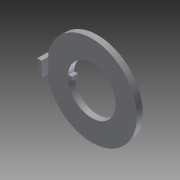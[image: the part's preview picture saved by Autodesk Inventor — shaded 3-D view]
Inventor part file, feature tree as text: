
AUTODESK INVENTOR PART (.ipt)
format: ipt  version: 2014 (Build 180170000, 170)  size: 108,032 bytes
history: native  units: in
note: dims shown in document units (in); Inventor stores cm internally (conversion verified against a paired STEP export)
features: other x7, extrude x2, sketch x2
ambient origin geometry x8: Origin, YZ Plane, XZ Plane, XY Plane, X Axis, Y Axis, Z Axis, Center Point
bodies: Solid1 (feature_tree)
feature tree (11):
  extrude  "Extrusion1"  Depth=0.079in TaperAngle=0.0deg
  extrude  "Extrusion2"  [1 undecoded]
  other  "ring_XY"
  other  "ring_YZ"
  other  "ring_ZX"
  other  "ring_X"
  other  "ring_Y"
  other  "ring_Z"
  other  "ring_Center"
  sketch  "Sketch_4"
  sketch  "Sketch_2"  dims[d0=0.031in d1=0.0in d2=0.079in d3=0.0in]
note: 1 required parameter value undecoded (feature->parameter linkage not recoverable at this tier; creation-order binding heuristic only, values carry confidence <= 0.55)
